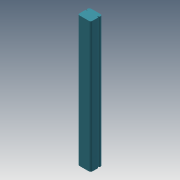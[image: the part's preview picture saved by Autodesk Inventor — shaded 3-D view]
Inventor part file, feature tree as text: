
AUTODESK INVENTOR PART (.ipt)
format: ipt  version: 2014 (Build 180170000, 170)  size: 126,464 bytes
history: native  units: mm
features: other x7, extrude x2, fillet x2, sketch x2, mirror x1
ambient origin geometry x8: Origin, YZ Plane, XZ Plane, XY Plane, X Axis, Y Axis, Z Axis, Center Point
bodies: Solid1 (feature_tree)
feature tree (14):
  other  "Table"
  other  "Rail-01"
  other  "Rail-04"
  other  "Rail-06"
  other  "Rail-05"
  other  "Rail-03"
  other  "Rail-02"
  extrude  "Extrusion1"  Depth=13.5mm
  extrude  "Extrusion2"  Depth=1.0mm
  mirror  "Mirror1"
  fillet  "Fillet1"  Radius=1.0mm
  fillet  "Fillet2"  Radius=0.5mm
  sketch  "Sketch1"  dims[d0=15.0mm d1=13.5mm]
  sketch  "Sketch2"  dims[d2=150.0mm d3=0.0mm d4=4.0mm d5=1.0mm d6=0.5mm d7=0.5mm d8=2.0mm d9=200.0mm d10=0.0mm d11=2.0mm d12=1.0mm]
